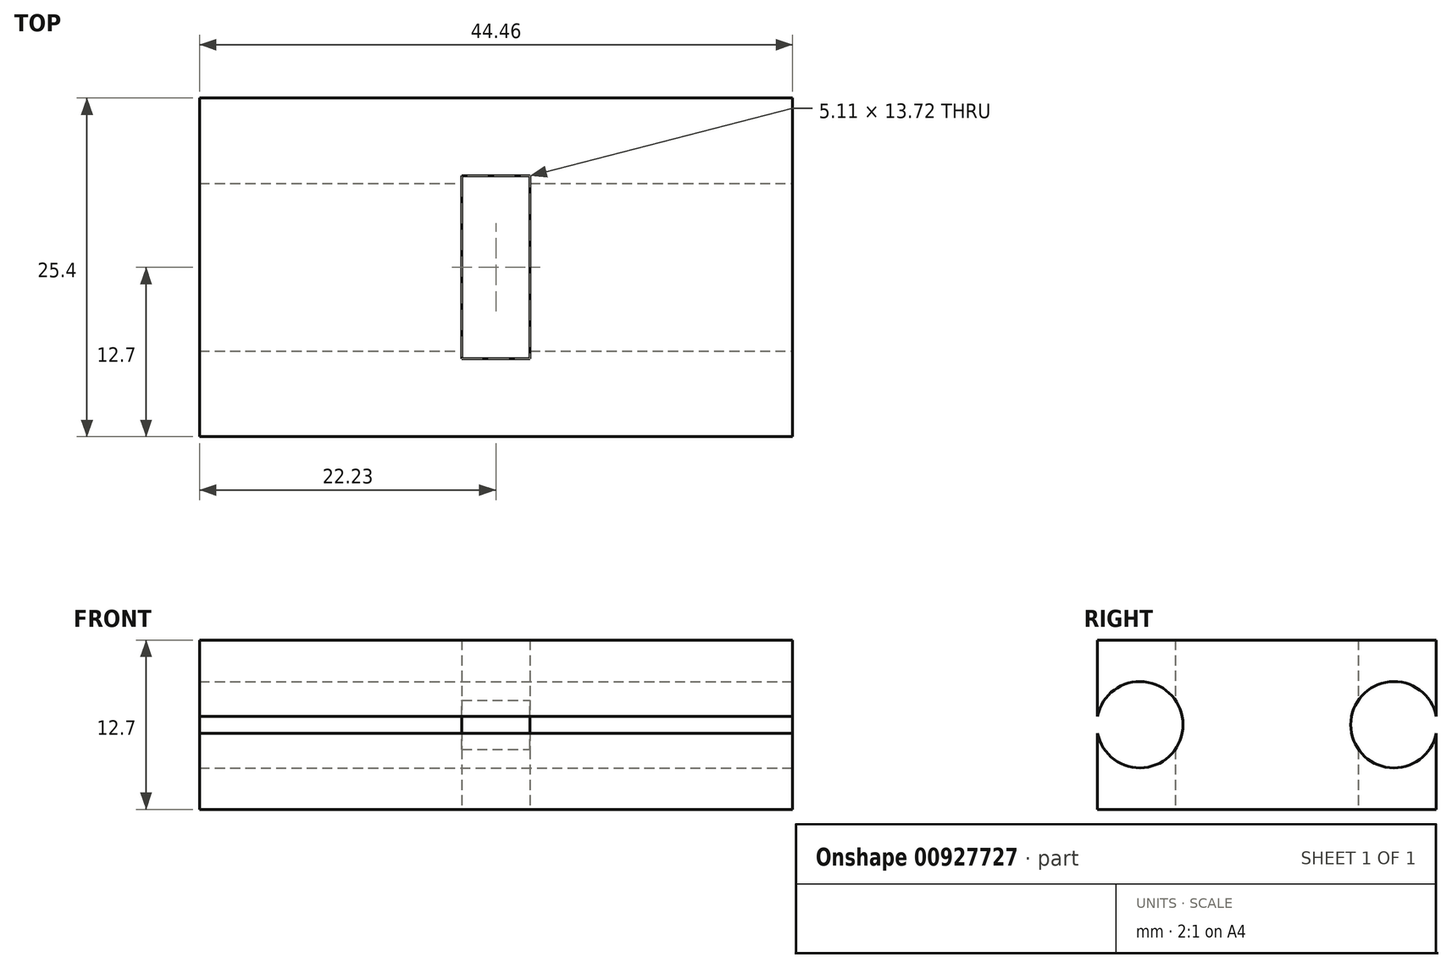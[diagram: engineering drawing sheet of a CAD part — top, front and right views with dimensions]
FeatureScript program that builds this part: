
annotation { "Feature Type Name" : "Feature", "Feature Type Description" : "" }
export const myFeature = defineFeature(function(context is Context, id is Id, definition is map)
    precondition{}
    {
        {
            var Q0;
            Q0=qCreatedBy(makeId("Top.planeOp"),FACE);
            var sketch = newSketch(context, id + "F0", { "sketchPlane" : qUnion([Q0])});
            skLineSegment(sketch, "E0.bottom", {"start": v(22.23, 12.7) * mm, "end": v(-22.23, 12.7) * mm});
            skLineSegment(sketch, "E0.top", {"start": v(22.23, -12.7) * mm, "end": v(-22.23, -12.7) * mm});
            skLineSegment(sketch, "E0.left", {"start": v(22.23, 12.7) * mm, "end": v(22.23, -12.7) * mm});
            skLineSegment(sketch, "E0.right", {"start": v(-22.23, 12.7) * mm, "end": v(-22.23, -12.7) * mm});
            skPoint(sketch, "E0.middle", {"position": v(0, 0) * mm});
            skLineSegment(sketch, "E1.bottom", {"start": v(-2.55, 6.86) * mm, "end": v(2.55, 6.86) * mm});
            skLineSegment(sketch, "E1.top", {"start": v(-2.55, -6.86) * mm, "end": v(2.55, -6.86) * mm});
            skLineSegment(sketch, "E1.left", {"start": v(-2.55, 6.86) * mm, "end": v(-2.55, -6.86) * mm});
            skLineSegment(sketch, "E1.right", {"start": v(2.55, 6.86) * mm, "end": v(2.55, -6.86) * mm});
            skSolve(sketch);
        }
        {
            var Q0;
            Q0=makeQuery(id+"F0.imprint","IMPRINT",FACE,{"disambiguationData":[TD([[makeQuery(id+"F0.imprint","IMPRINT",EDGE,{"derivedFrom":sQuery(id+"F0.wireOp",EDGE,"E0.bottom")}),1.0]])]});
            extrude(context, id + "F1", {"entities" : qUnion([Q0]), "depth" : 12.7 * mm, "offsetDistance" : 25.4 * mm});
        }
        {
            var Q0;
            Q0=makeQuery(id+"F1.opExtrude","SWEPT_FACE",FACE,{"disambiguationData":[OSD([sQuery(id+"F0.wireOp",EDGE,"E0.left")])]});
            var sketch = newSketch(context, id + "F2", { "sketchPlane" : qUnion([Q0])});
            skPoint(sketch, "E2", {"position": v(-9.52, 6.35) * mm});
            skPoint(sketch, "E3", {"position": v(9.53, 6.35) * mm});
            skSolve(sketch);
        }
        {
            var Q0;
            Q0=sQuery(id+"F2.wireOp",VERTEX,"E2");
            var Q1;
            Q1=sQuery(id+"F2.wireOp",VERTEX,"E3");
            var Q2;
            Q2=makeQuery(id+"F1.opExtrude","SWEPT_BODY",BODY,{"disambiguationData":[OSD([sQuery(id+"F0.wireOp",EDGE,"E0.bottom"),sQuery(id+"F0.wireOp",EDGE,"E0.top"),sQuery(id+"F0.wireOp",EDGE,"E0.left"),sQuery(id+"F0.wireOp",EDGE,"E0.right")])]});
            hole(context, id + "F3", {"style" : HoleStyle.SIMPLE, "endStyle" : HoleEndStyle.THROUGH, "holeDiameter" : 6.48 * mm, "majorDiameter" : 6.35 * mm, "isTappedThrough" : true, "tappedDepth" : 12.7 * mm, "tapClearance" : 3, "locations" : qUnion([Q0, Q1]), "scope" : qUnion([Q2])});
        }
    });
